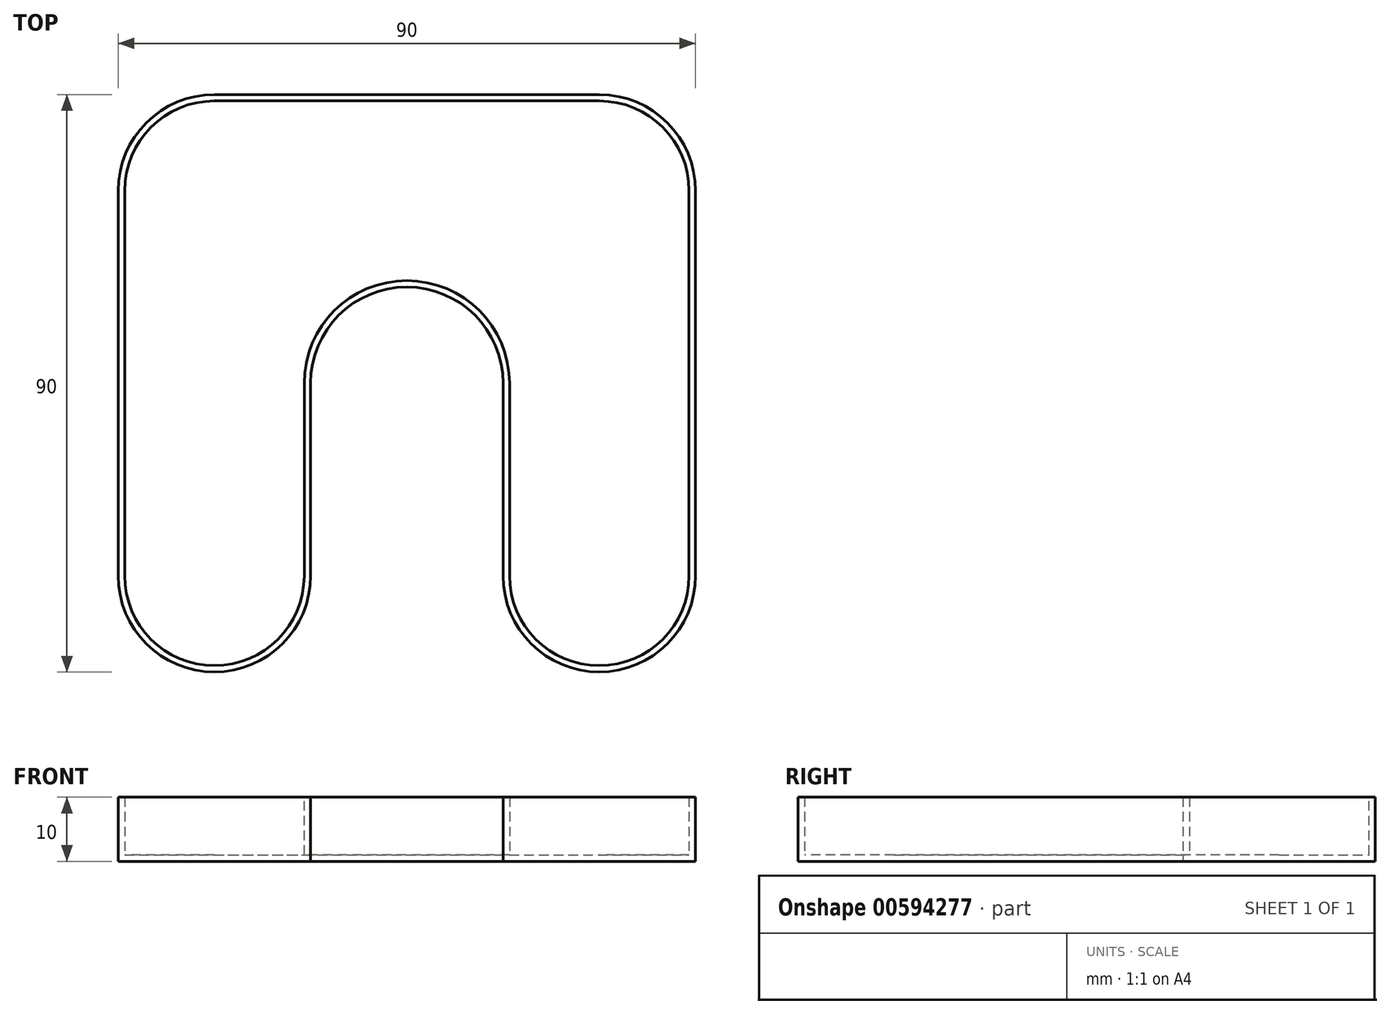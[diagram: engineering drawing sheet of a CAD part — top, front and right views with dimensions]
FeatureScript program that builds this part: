
annotation { "Feature Type Name" : "Feature", "Feature Type Description" : "" }
export const myFeature = defineFeature(function(context is Context, id is Id, definition is map)
    precondition{}
    {
        {
            var Q0;
            Q0=qCreatedBy(makeId("Top.planeOp"),FACE);
            var sketch = newSketch(context, id + "F0", { "sketchPlane" : qUnion([Q0])});
            skLineSegment(sketch, "E0.bottom", {"start": v(-30, 45) * mm, "end": v(30, 45) * mm});
            skLineSegment(sketch, "E0.top", {"start": v(-30, -45) * mm, "end": v(-30, -45) * mm});
            skLineSegment(sketch, "E0.left", {"start": v(-45, 30) * mm, "end": v(-45, -30) * mm});
            skLineSegment(sketch, "E0.right", {"start": v(45, 30) * mm, "end": v(45, -30) * mm});
            skPoint(sketch, "E0.middle", {"position": v(0, 0) * mm});
            skLineSegment(sketch, "E1.trimOffspring", {"start": v(30, -45) * mm, "end": v(30, -45) * mm});
            skLineSegment(sketch, "E2", {"start": v(-15, -30) * mm, "end": v(-15, 0) * mm});
            skLineSegment(sketch, "E3", {"start": v(0, 15) * mm, "end": v(0, 15) * mm});
            skLineSegment(sketch, "E4", {"start": v(15, 0) * mm, "end": v(15, -30) * mm});
            skPoint(sketch, "E5.visualSharp", {"position": v(-45, 45) * mm});
            skArc(sketch, "E5.filletArc", {"start": v(-30, 45) * mm, "mid": v(-40.6, 40.6) * mm, "end": v(-45, 30) * mm});
            skPoint(sketch, "E6.visualSharp", {"position": v(-45, -45) * mm});
            skArc(sketch, "E6.filletArc", {"start": v(-45, -30) * mm, "mid": v(-40.6, -40.6) * mm, "end": v(-30, -45) * mm});
            skPoint(sketch, "E7.visualSharp", {"position": v(-15, -45) * mm});
            skArc(sketch, "E7.filletArc", {"start": v(-30, -45) * mm, "mid": v(-19.4, -40.6) * mm, "end": v(-15, -30) * mm});
            skPoint(sketch, "E8.visualSharp", {"position": v(15, 15) * mm});
            skArc(sketch, "E8.filletArc", {"start": v(15, 0) * mm, "mid": v(10.6, 10.6) * mm, "end": v(0, 15) * mm});
            skPoint(sketch, "E9.visualSharp", {"position": v(-15, 15) * mm});
            skArc(sketch, "E9.filletArc", {"start": v(0, 15) * mm, "mid": v(-10.6, 10.6) * mm, "end": v(-15, 0) * mm});
            skPoint(sketch, "E10.visualSharp", {"position": v(15, -45) * mm});
            skArc(sketch, "E10.filletArc", {"start": v(15, -30) * mm, "mid": v(19.4, -40.6) * mm, "end": v(30, -45) * mm});
            skPoint(sketch, "E11.visualSharp", {"position": v(45, -45) * mm});
            skArc(sketch, "E11.filletArc", {"start": v(30, -45) * mm, "mid": v(40.6, -40.6) * mm, "end": v(45, -30) * mm});
            skPoint(sketch, "E12.visualSharp", {"position": v(45, 45) * mm});
            skArc(sketch, "E12.filletArc", {"start": v(45, 30) * mm, "mid": v(40.6, 40.6) * mm, "end": v(30, 45) * mm});
            skSolve(sketch);
        }
        {
            var Q0;
            Q0 = qSketchRegion(id + "F0", true);
            extrude(context, id + "F1", {"entities" : qUnion([Q0]), "depth" : 10 * mm, "offsetDistance" : 25 * mm});
        }
        {
            var Q0;
            Q0=makeQuery(id+"F1.opExtrude","CAP_FACE",FACE,{"disambiguationData":[OSD([sQuery(id+"F0.wireOp",EDGE,"E0.bottom"),sQuery(id+"F0.wireOp",EDGE,"E0.left"),sQuery(id+"F0.wireOp",EDGE,"E0.right"),sQuery(id+"F0.wireOp",EDGE,"E2"),sQuery(id+"F0.wireOp",EDGE,"E4"),sQuery(id+"F0.wireOp",EDGE,"E5.filletArc"),sQuery(id+"F0.wireOp",EDGE,"E6.filletArc"),sQuery(id+"F0.wireOp",EDGE,"E7.filletArc"),sQuery(id+"F0.wireOp",EDGE,"E8.filletArc"),sQuery(id+"F0.wireOp",EDGE,"E9.filletArc"),sQuery(id+"F0.wireOp",EDGE,"E10.filletArc"),sQuery(id+"F0.wireOp",EDGE,"E11.filletArc"),sQuery(id+"F0.wireOp",EDGE,"E12.filletArc")])],"isStart":false});
            shell(context, id + "F2", {"entities" : qUnion([Q0]), "thickness" : 1 * mm});
        }
    });
